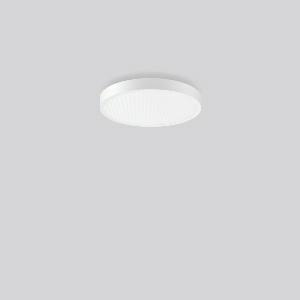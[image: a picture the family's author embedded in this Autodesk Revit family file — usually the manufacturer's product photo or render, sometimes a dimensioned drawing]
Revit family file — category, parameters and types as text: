
# Revit family: triona_round_a_312424_002_76_9569
name_source: partatom
category: Lighting Fixtures
units: mm (PartAtom-declared; Revit-internal decimal feet)

## family parameters
Cut with Voids When Loaded = No
Host = Face
Light Source = No
Part Type = Normal
Room Calculation Point = No
Round Connector Dimension = Use Diameter
Shared = No

## types (1)
- TRIONA round A (1 x LED Modul 830, 3700 lm, 3000)
    Apparent Load = 38 VA
    CIE Flux Codes = 58 87 97 82 100
    Color Rendering = 80
    Color Temperature = 3000
    Default Elevation = 1800 mm
    Description = Series: TRIONA round
Decorative round LED surface-mounted luminaire. Flat, seamless frame: aluminium extrusion profile, powder coated. Cover made of sheet steel, powder-coated. Direct light emission through a diffuser plastic opal/prismatic. Indirect light emission through a flush diffuser made of satin-finish plastic. Lightguide and diffuser made of non-yellowing plastic (PMMA). Lateral light emission (RZB SIDELITE technology) for above-average homogeneous light distribution. Direct 70%, indirect 30% light emission. Suitable for Ceiling mounting, Wall (surface). Tool-free mounting via bayonet connection. Electronic ballast included. Very easy installation thanks to Plug+Play connection. Perfect for office areas (RUG < 19) and environments with computer screens in accordance with EN 12464-1. 
Colour: traffic white, matt (RAL 9016)
Diameter: 461 mm
Height: 88 mm
Lamp: LED
Socket: without socket
Colour temperature: 3000K
Colour rendering index (CRI): 80
System power: 38 W
Rated luminous flux: 3700 lm
Luminous efficiency: 97 lm/W
Control gear: Converter, dimmable, DALI
Protection class: I
Type of protection: IP 20
    Height = 88 mm
    Lamp = 1 x LED Modul 830
    Lamp Light Flux = 3700 lm
    Lamp count = 1
    Length = 461 mm
    Lifetime = 50000 h
    Luminous efficacy = 97 lm/W
    Manufacturer = RZB
    ModVariant = No
    Model = 312424.002.76
    Mounting Place = Ceiling
    Mounting Type = Surface mounted
    Number of Poles = 1
    OnlyDefault = Yes
    Power Factor = 1
    Product Name = TRIONA round A
    Product group = Surface mounted modular luminaires
    ProductGroupID = 306
    Protection Class = Protection class I
    Protection Degree = IP 20
    RLX_Detail_Level = 1
    RLX_Emergency_Light_Flux = 0 lm
    RLX_Emergency_Type = 0
    RLX_Emergency_Type_DB = No
    RlxData = <blob elided: 37273 chars, md5=f7e7d1e1>
    Socket = socket
    Standby Power = 0 W
    System Light Flux = 3700 lm
    System Power = 38 W
    Type Comments = Product without accessories
    Type Image = 312424.002.jpg
    URL = http://relux.com
    VarID = ---
    Voltage = 230 V
    Voltage Range = 220-240 V
    Weight = 0.00 kg
    Width = 0 mm  [stored 0 ft]

note: [stored X ft] marks values corroborated as IEEE doubles in the binary element streams (Revit-internal decimal feet)

## geometry (parser evidence)
native form markers: Blend x4, Sweep x12
no freeform markers — native parametric forms only
